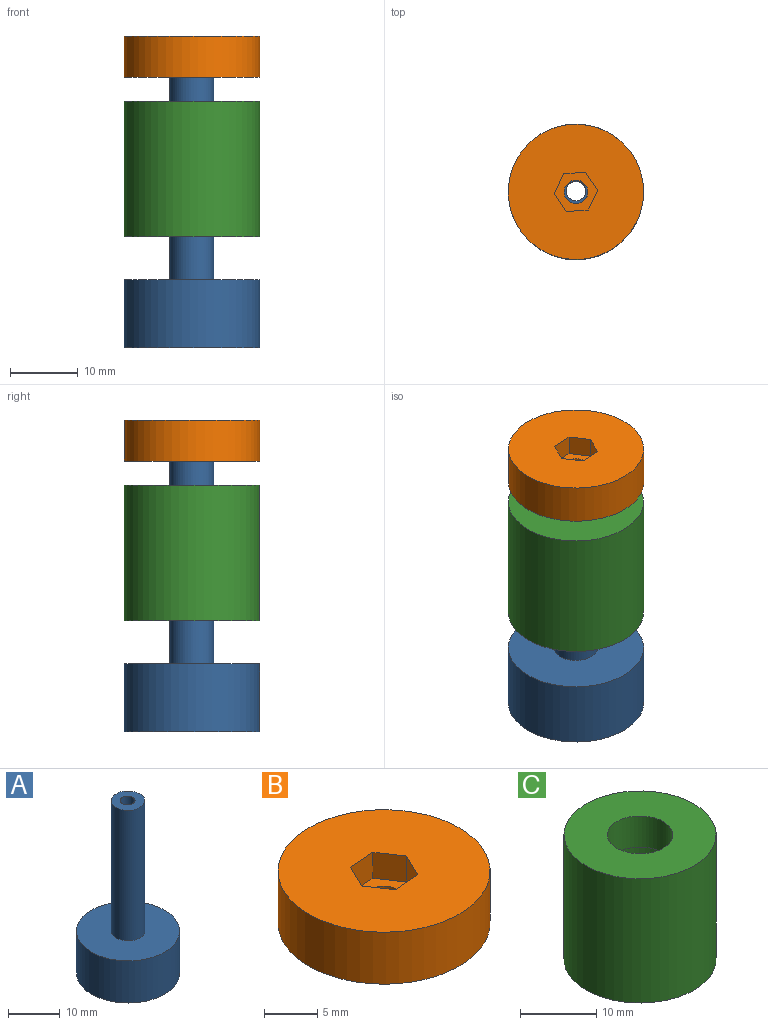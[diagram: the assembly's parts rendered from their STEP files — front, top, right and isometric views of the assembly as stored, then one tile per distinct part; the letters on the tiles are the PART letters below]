
ASSEMBLY  parts=3 mates=2
PART A: 8 faces, bbox 20x20x41 mm
  f0: cylinder r=1.45mm len=37.9mm, axis (0,0,-1), area 345.3mm2, adj f5,f7
  f1: cylinder r=10mm len=20mm, axis (0,0,-1), area 628.3mm2, adj f2,f3
  f2: plane 20x20mm, normal (0,0,1), area 281mm2, adj f1,f4
  f3: plane 20x20mm, normal (0,0,-1), area 125.5mm2, adj f1,f6
  f4: cylinder r=3.25mm len=31mm, axis (0,0,-1), area 633mm2, adj f2,f5
  f5: plane 6.5x6.5mm, normal (0,0,1), area 26.6mm2, adj f0,f4
  f6: cylinder r=7.75mm len=15.5mm, axis (0,0,-1), area 151mm2, adj f3,f7
  f7: plane 15.5x15.5mm, normal (0,0,-1), area 182.1mm2, adj f0,f6
PART B: 13 faces, bbox 20x20x6 mm
  f0: cylinder r=1.75mm len=3.5mm, axis (0,0,-1), area 22mm2, adj f5,f12
  f1: cylinder r=10mm len=20mm, axis (0,0,-1), area 377mm2, adj f2,f3
  f2: plane 20x20mm, normal (0,0,1), area 287mm2, adj f1,f6,f7,f8,f9,f10,f11
  f3: plane 20x20mm, normal (0,0,-1), area 260.1mm2, adj f1,f4
  f4: cylinder r=4.15mm len=8.3mm, axis (0,0,-1), area 26.1mm2, adj f3,f5
  f5: plane 8.3x8.3mm, normal (0,0,-1), area 44.5mm2, adj f0,f4
  f6: plane 3x2.9mm, normal (-0.9,0.44,0), area 9.7mm2, adj f2,f7,f11,f12
  f7: plane 3x2.68mm, normal (-0.83,-0.56,0), area 9.7mm2, adj f2,f6,f8,f12
  f8: plane 3.23x3mm, normal (0.07,-1,0), area 9.7mm2, adj f2,f7,f9,f12
  f9: plane 3x2.9mm, normal (0.9,-0.44,0), area 9.7mm2, adj f2,f8,f10,f12
  f10: plane 3x2.68mm, normal (0.83,0.56,0), area 9.7mm2, adj f2,f9,f11,f12
  f11: plane 3.23x3mm, normal (-0.07,1,0), area 9.7mm2, adj f2,f6,f10,f12
  f12: plane 6.45x5.81mm, normal (0,0,1), area 17.5mm2, adj f0,f6,f7,f8,f9,f10,f11
PART C: 6 faces, bbox 20x20x20 mm
  f0: plane 12x12mm, normal (0,0,-1), area 55mm2, adj f1,f4
  f1: cylinder r=4.3mm len=8.6mm, axis (0,0,-1), area 135.1mm2, adj f0,f3
  f2: cylinder r=10mm len=20mm, axis (0,0,-1), area 1256.6mm2, adj f3,f5
  f3: plane 20x20mm, normal (0,0,1), area 256.1mm2, adj f1,f2
  f4: cylinder r=6mm len=15mm, axis (0,0,1), area 565.5mm2, adj f0,f5
  f5: plane 20x20mm, normal (0,0,-1), area 201.1mm2, adj f2,f4
PLACE A t=(-1.35,6.42,-6.7)mm fixed
PLACE B t=(-1.35,6.39,33.3)mm
PLACE C t=(-1.35,6.42,24.7)mm
MATE slider A.f4 <-> C.f4  axis (0,0,-1) through (-1.35,6.42,18.8)mm
MATE fastened B.f4 <-> A.f5  axis (0,0,-1) through (-1.35,6.39,34.3)mm
